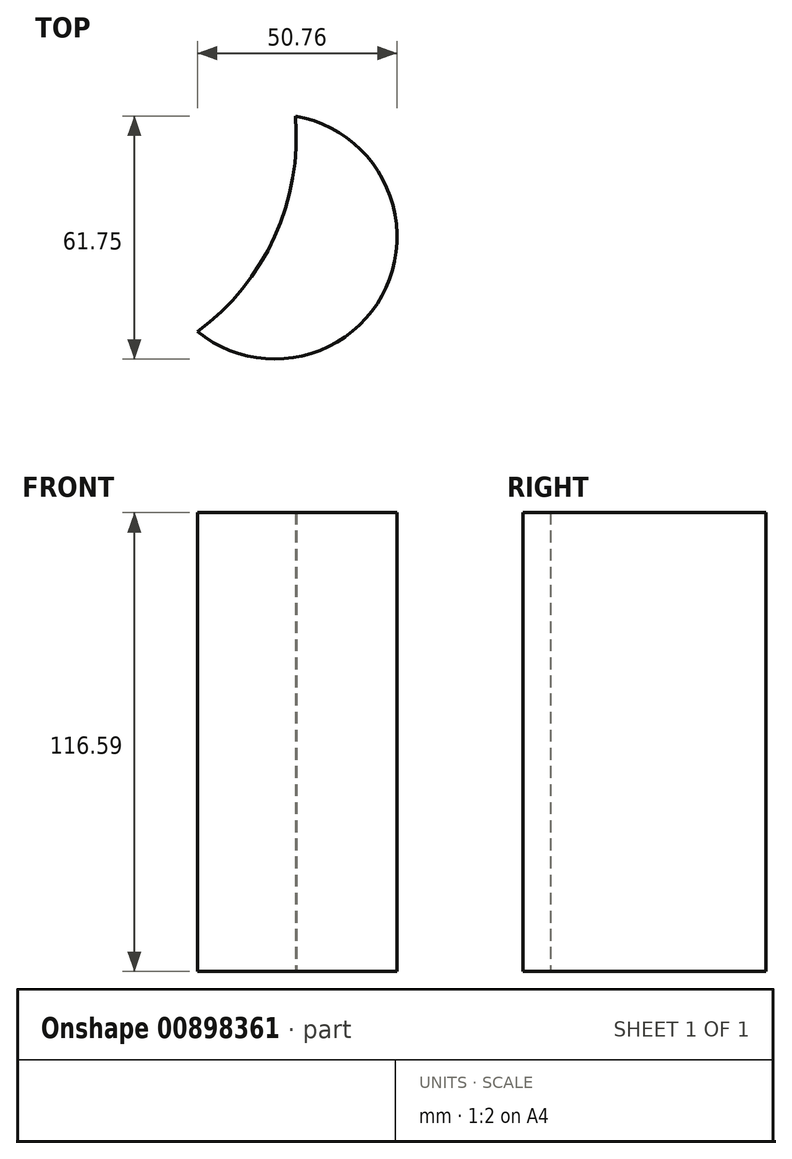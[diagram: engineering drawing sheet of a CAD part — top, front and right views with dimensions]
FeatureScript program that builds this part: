
annotation { "Feature Type Name" : "Feature", "Feature Type Description" : "" }
export const myFeature = defineFeature(function(context is Context, id is Id, definition is map)
    precondition{}
    {
        {
            var Q0;
            Q0=qCreatedBy(makeId("Top.planeOp"),FACE);
            var sketch = newSketch(context, id + "F0", { "sketchPlane" : qUnion([Q0])});
            skCircle(sketch, "E0", {"center": v(0, 0) * mm, "radius": 61.15 * mm});
            skCircle(sketch, "E1", {"center": v(55.66, -25.32) * mm, "radius": 31.1 * mm});
            skSolve(sketch);
        }
        {
            var Q0;
            {var subQ0=sQuery(id+"F0.wireOp",EDGE,"E1");var subQ1=sQuery(id+"F0.wireOp",EDGE,"E0");var subQ2=makeQuery(id+"F0.imprint","INTERSECT",VERTEX,{"disambiguationData":[OD(0.0)],"derivedFrom":[subQ1,subQ0]});Q0=makeQuery(id+"F0.imprint","IMPRINT",FACE,{"disambiguationData":[TD([[makeQuery(id+"F0.imprint","IMPRINT",EDGE,{"disambiguationData":[TD([[subQ2,-1.0]])],"derivedFrom":subQ1}),-1.0]])]});}
            extrude(context, id + "F1", {"entities" : qUnion([Q0]), "depth" : 116.6 * mm, "offsetDistance" : 25.4 * mm});
        }
    });
